# Revit family: RN 81050 Optipress-Aquaplus-Gomito
name_source: partatom
category: Rohrformteile
units: mm (PartAtom-declared; Revit-internal decimal feet)

## family parameters
Arbeitsebenenbasiert = Nein
Beim Laden mit Abzugskörper schneiden = Nein
Bemaßung runder Anschluss = Durchmesser verwenden
Gemeinsam genutzt = Nein
Immer vertikal = Ja
Teiletyp = Nicht definiert

## types (6) — shared parameters
1.010.00.2 Number of the part of the guideline = 29
1.010.00.3 Issue date (month) of the guideline = 201308
1.010.00.4 Manufacturer name = R. Nussbaum AG
1.010.00.5 Revision date of the file = 20190521
1.100.00.4 Product designation = Fornitura
1.110.00.2 Index = 4
1.110.00.4 Product designation = Optipress
1.960/3L.00.8 Link (URL) = https://www.nussbaum.ch
29.700.00.4 Product name = Optipress-Aquaplus-Gomito, con flangia murale
29.700.00.5 Product identification = 2
29.700.00.6 Cross-sectional shape = 1
29.700.00.7 Nominal size system = DN
29.700.00.8 Nominal pressure system = PN
29.710.02.4 Nominal pressure = 16
29.710.02.5 max. allowed overpressure [hPa] = 1600
29.710.02.7 max. allowed continuous operating pressure [hPa] = 1600
29.710.02.9 max. allowed continuous operating temperature [°C] = 95
Connector Visibility = Nein
EnclosingSpace Visibility = Nein

## per-type parameters (varying)
| type | 1.800.00.3 BS number | 1.810.00.3 Manufacturer’s reference number | 1.810.00.4 DATANORM number | 1.810.00.5 StLB number | 1.810.00.6 GTIN number | 29.710.02.10 Fitting weight [kg] | 29.710.02.3 Designation | CONNECTOR0_DIAMETER_dZ_0r | CONNECTOR0_dZ_00 | CONNECTOR0_dZ_01 | CONNECTOR0_ref_dX | CONNECTOR0_ref_dZ | CONNECTOR1_DIAMETER_dX_0r | CONNECTOR1_dX_00 | CONNECTOR1_dX_01 | CONNECTOR1_ref_dX | R. Nussbaum AG 81050.20 it Visibility | R. Nussbaum AG 81050.21 it Visibility | R. Nussbaum AG 81050.22 it Visibility | R. Nussbaum AG 81050.23 it Visibility | R. Nussbaum AG 81050.24 it Visibility | R. Nussbaum AG 81050.25 it Visibility |
| 81050.21, Optipress-Aquaplus-Gomito, con flangia murale, DN=12x15, L=46, Rp=½ | 01900400000000000000000000000000000000000000000032000000000000000006 | 81050.21 | 81050.21 | 263.112 | 7612945022523 | 0.119 | Optipress-Aquaplus-Gomito, con flangia murale, DN=12x15, L=46, Rp=½ | 12 mm  [stored 0.0393701 ft] | 43 mm | 21 mm | 13 mm | 21 mm | 15 mm | 22 mm | 35 mm | 22 mm | Nein | Ja | Nein | Nein | Nein | Nein |
| 81050.22, Optipress-Aquaplus-Gomito, con flangia murale, DN=15, L=46, Rp=½ | 01900400000000000000000000000000000000000000000032000000000000000007 | 81050.22 | 81050.22 | 263.113 | 7612945022530 | 0.123 | Optipress-Aquaplus-Gomito, con flangia murale, DN=15, L=46, Rp=½ | 13 mm | 43 mm | 21 mm | 14 mm  [stored 0.0459318 ft] | 21 mm | 15 mm | 23 mm | 36 mm | 23 mm | Nein | Nein | Ja | Nein | Nein | Nein |
| 81050.23, Optipress-Aquaplus-Gomito, con flangia murale, DN=15x20, L=50, Rp=¾ | 01900400000000000000000000000000000000000000000032000000000000000008 | 81050.23 | 81050.23 |  | 7612945022547 | 0.185 | Optipress-Aquaplus-Gomito, con flangia murale, DN=15x20, L=50, Rp=¾ | 11 mm | 50 mm | 28 mm | 16 mm | 28 mm | 20 mm | 25 mm  [stored 0.082021 ft] | 40 mm | 25 mm  [stored 0.082021 ft] | Nein | Nein | Nein | Ja | Nein | Nein |
| 81050.24, Optipress-Aquaplus-Gomito, con flangia murale, DN=20x15, L=52, Rp=½ | 01900400000000000000000000000000000000000000000032000000000000000009 | 81050.24 | 81050.24 |  | 7612945022554 | 0.161 | Optipress-Aquaplus-Gomito, con flangia murale, DN=20x15, L=52, Rp=½ | 16 mm | 50 mm | 26 mm | 18 mm | 26 mm | 15 mm | 29 mm | 42 mm | 29 mm | Nein | Nein | Nein | Nein | Ja | Nein |
| 81050.25, Optipress-Aquaplus-Gomito, con flangia murale, DN=20, L=52, Rp=¾ | 01900400000000000000000000000000000000000000000032000000000000000010 | 81050.25 | 81050.25 | 263.114 | 7612945022561 | 0.191 | Optipress-Aquaplus-Gomito, con flangia murale, DN=20, L=52, Rp=¾ | 19 mm | 50 mm | 26 mm | 19 mm | 26 mm | 20 mm | 31 mm | 46 mm | 31 mm | Nein | Nein | Nein | Nein | Nein | Ja |
| 81050.20, Optipress-Aquaplus-Gomito, con flangia murale, DN=10x15, L=40, Rp=½ | 01900400000000000000000000000000000000000000000032000000000000000011 | 81050.20 | 81050.20 | 263.111 | 7612945022516 | 0.113 | Optipress-Aquaplus-Gomito, con flangia murale, DN=10x15, L=40, Rp=½ | 10 mm  [stored 0.0328084 ft] | 40 mm | 22 mm | 11 mm | 22 mm | 15 mm | 18 mm | 31 mm | 18 mm | Ja | Nein | Nein | Nein | Nein | Nein |

note: column(s) folded — value = type name in every type: 1.800.00.4 Comment field

note: [stored X ft] marks values corroborated as IEEE doubles in the binary element streams (Revit-internal decimal feet)

## geometry (parser evidence)
native form markers: Sweep x3
no freeform markers — native parametric forms only
